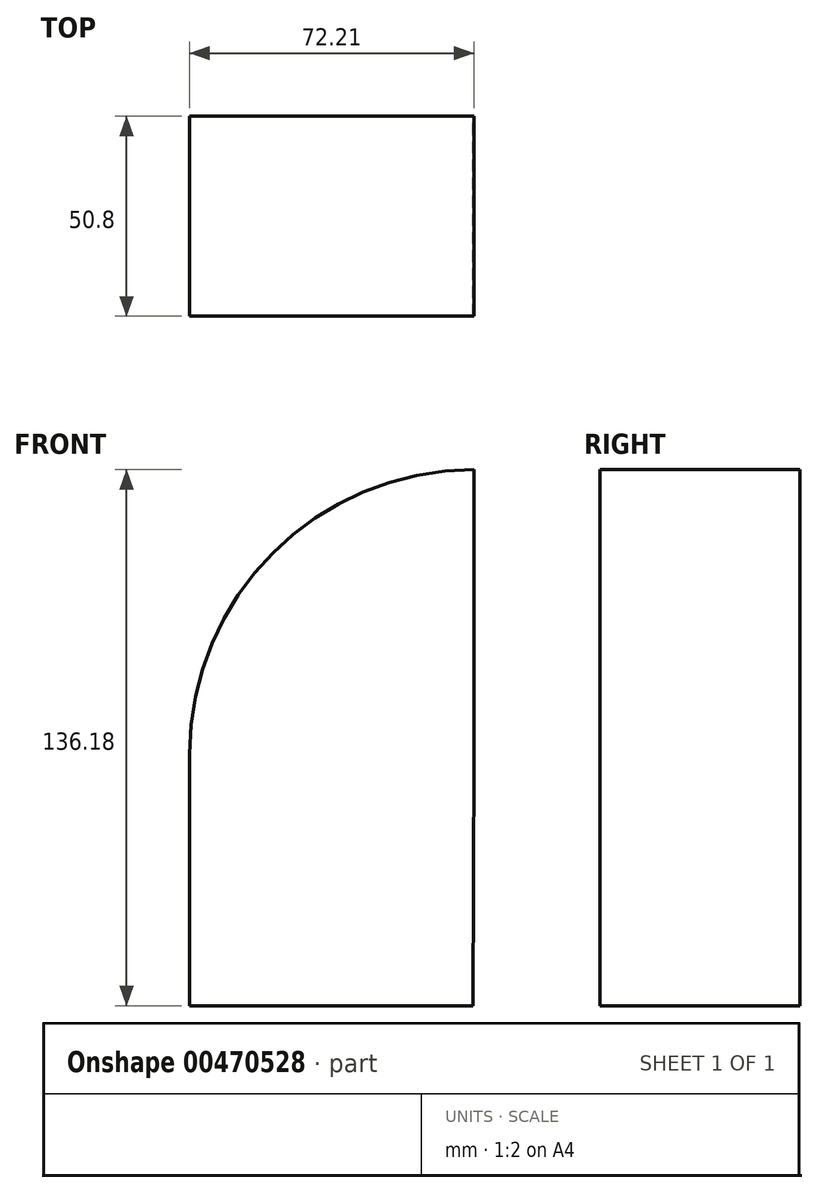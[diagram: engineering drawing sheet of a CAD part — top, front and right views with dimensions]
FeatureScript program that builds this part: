
annotation { "Feature Type Name" : "Feature", "Feature Type Description" : "" }
export const myFeature = defineFeature(function(context is Context, id is Id, definition is map)
    precondition{}
    {
        {
            var Q0;
            Q0=qCreatedBy(makeId("Front.planeOp"),FACE);
            var sketch = newSketch(context, id + "F0", { "sketchPlane" : qUnion([Q0])});
            skLineSegment(sketch, "E0", {"start": v(0, 0) * mm, "end": v(0, 63.97) * mm});
            skLineSegment(sketch, "E1", {"start": v(71.95, 0) * mm, "end": v(0, 0) * mm});
            skLineSegment(sketch, "E2", {"start": v(0, 63.97) * mm, "end": v(72.21, 63.97) * mm});
            skLineSegment(sketch, "E3", {"start": v(72.21, 63.97) * mm, "end": v(71.95, 0) * mm});
            skSolve(sketch);
        }
        {
            var Q0;
            Q0=makeQuery(id+"F0.imprint","IMPRINT",FACE,{"disambiguationData":[TD([[makeQuery(id+"F0.imprint","IMPRINT",EDGE,{"derivedFrom":sQuery(id+"F0.wireOp",EDGE,"E0")}),-1.0]])]});
            extrude(context, id + "F1", {"entities" : qUnion([Q0]), "endBound" : BoundingType.SYMMETRIC, "depth" : 50.8 * mm});
        }
        {
            var Q0;
            Q0=makeQuery(id+"F1.opExtrude","SWEPT_FACE",FACE,{"disambiguationData":[OSD([sQuery(id+"F0.wireOp",EDGE,"E2")])]});
            var Q1;
            Q1=makeQuery(id+"F1.opExtrude","SWEPT_EDGE",EDGE,{"disambiguationData":[OSD([sQuery(id+"F0.wireOp",EDGE,"E2"),sQuery(id+"F0.wireOp",EDGE,"E3")])]});
            revolve(context, id + "F2", {"operationType" : NewBodyOperationType.ADD, "entities" : qUnion([Q0]), "axis" : qUnion([Q1]), "revolveType" : RevolveType.ONE_DIRECTION, "angle" : 90 * degree});
        }
    });
